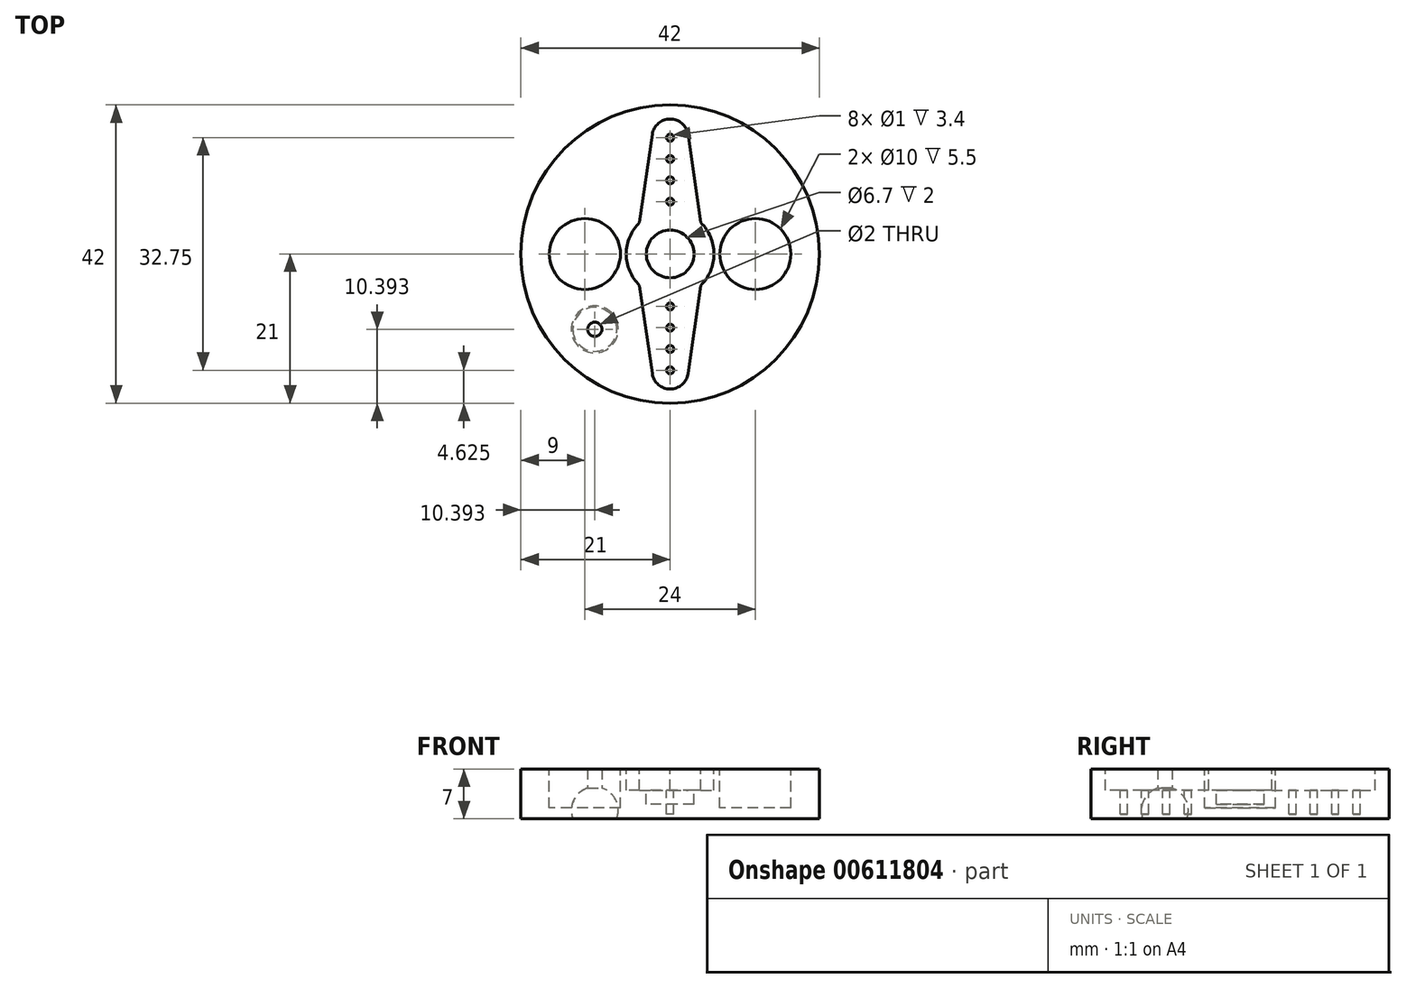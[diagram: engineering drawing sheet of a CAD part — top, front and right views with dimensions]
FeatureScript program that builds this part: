
annotation { "Feature Type Name" : "Feature", "Feature Type Description" : "" }
export const myFeature = defineFeature(function(context is Context, id is Id, definition is map)
    precondition{}
    {
        {
            var Q0;
            Q0=qCreatedBy(makeId("Top.planeOp"),FACE);
            var sketch = newSketch(context, id + "F0", { "sketchPlane" : qUnion([Q0])});
            skCircle(sketch, "E0", {"center": v(0, 0) * mm, "radius": 21 * mm});
            skSolve(sketch);
        }
        {
            var Q0;
            Q0=makeQuery(id+"F0.imprint","IMPRINT",FACE,{"disambiguationData":[TD([[makeQuery(id+"F0.imprint","IMPRINT",EDGE,{"derivedFrom":sQuery(id+"F0.wireOp",EDGE,"E0")}),1.0]])]});
            extrude(context, id + "F1", {"entities" : qUnion([Q0]), "depth" : 7 * mm, "offsetDistance" : 25 * mm});
        }
        {
            var Q0;
            Q0=makeQuery(id+"F1.opExtrude","CAP_FACE",FACE,{"disambiguationData":[OSD([sQuery(id+"F0.wireOp",EDGE,"E0")])],"isStart":false});
            var sketch = newSketch(context, id + "F2", { "sketchPlane" : qUnion([Q0])});
            skArc(sketch, "E1", {"start": v(-4.3, 4.43) * mm, "mid": v(-6.17, 0) * mm, "end": v(-4.3, -4.43) * mm});
            skLineSegment(sketch, "E2", {"start": v(0, 19) * mm, "end": v(0, -19) * mm, "construction": true});
            skLineSegment(sketch, "E3", {"start": v(-4.3, 4.43) * mm, "end": v(-2.5, 16.86) * mm});
            skLineSegment(sketch, "E4", {"start": v(-4.3, 4.43) * mm, "end": v(0, 4.43) * mm, "construction": true});
            skLineSegment(sketch, "E5", {"start": v(-2.5, 16.86) * mm, "end": v(0, 16.86) * mm, "construction": true});
            skArc(sketch, "E6", {"start": v(0, 19) * mm, "mid": v(-1.65, 18.4) * mm, "end": v(-2.5, 16.86) * mm});
            skLineSegment(sketch, "E7.MirrorCS", {"start": v(4.3, 4.43) * mm, "end": v(2.5, 16.86) * mm});
            skArc(sketch, "E8.MirrorCS", {"start": v(0, 19) * mm, "mid": v(1.65, 18.4) * mm, "end": v(2.5, 16.86) * mm});
            skLineSegment(sketch, "E9", {"start": v(-21, 0) * mm, "end": v(21, 0) * mm, "construction": true});
            skLineSegment(sketch, "E10.MirrorCS", {"start": v(-4.3, -4.43) * mm, "end": v(-2.5, -16.86) * mm});
            skLineSegment(sketch, "E11.MirrorCS", {"start": v(4.3, -4.43) * mm, "end": v(2.5, -16.86) * mm});
            skArc(sketch, "E12.MirrorCS", {"start": v(0, -19) * mm, "mid": v(-1.65, -18.4) * mm, "end": v(-2.5, -16.86) * mm});
            skArc(sketch, "E13.MirrorCS", {"start": v(0, -19) * mm, "mid": v(1.65, -18.4) * mm, "end": v(2.5, -16.86) * mm});
            skArc(sketch, "E14.trimOffspring", {"start": v(4.3, -4.43) * mm, "mid": v(6.17, 0) * mm, "end": v(4.3, 4.43) * mm});
            skSolve(sketch);
        }
        {
            var Q0;
            Q0 = qSketchRegion(id + "F2", true);
            extrude(context, id + "F3", {"entities" : qUnion([Q0]), "operationType" : NewBodyOperationType.REMOVE, "oppositeDirection" : true, "depth" : 3 * mm, "offsetDistance" : 25 * mm});
        }
        {
            var Q0;
            Q0=makeQuery(id+"F3.boolean.opBoolean","COPY",FACE,{"derivedFrom":makeQuery(id+"F3.opExtrude","CAP_FACE",FACE,{"disambiguationData":[OSD([sQuery(id+"F2.wireOp",EDGE,"E1"),sQuery(id+"F2.wireOp",EDGE,"E3"),sQuery(id+"F2.wireOp",EDGE,"E6"),sQuery(id+"F2.wireOp",EDGE,"E7.MirrorCS"),sQuery(id+"F2.wireOp",EDGE,"E8.MirrorCS"),sQuery(id+"F2.wireOp",EDGE,"E10.MirrorCS"),sQuery(id+"F2.wireOp",EDGE,"E11.MirrorCS"),sQuery(id+"F2.wireOp",EDGE,"E12.MirrorCS"),sQuery(id+"F2.wireOp",EDGE,"E13.MirrorCS"),sQuery(id+"F2.wireOp",EDGE,"E14.trimOffspring")])],"isStart":false})});
            var sketch = newSketch(context, id + "F4", { "sketchPlane" : qUnion([Q0])});
            skArc(sketch, "E15.0", {"start": v(-4.3, 4.43) * mm, "mid": v(-6.17, 0) * mm, "end": v(-4.3, -4.43) * mm, "construction": true});
            skArc(sketch, "E15.1", {"start": v(4.3, -4.43) * mm, "mid": v(6.17, 0) * mm, "end": v(4.3, 4.43) * mm, "construction": true});
            skCircle(sketch, "E16", {"center": v(0, 0) * mm, "radius": 3.35 * mm});
            skSolve(sketch);
        }
        {
            var Q0;
            Q0 = qSketchRegion(id + "F4", true);
            extrude(context, id + "F5", {"entities" : qUnion([Q0]), "operationType" : NewBodyOperationType.REMOVE, "oppositeDirection" : true, "depth" : 2 * mm, "offsetDistance" : 25 * mm});
        }
        {
            var Q0;
            Q0=makeQuery(id+"F3.boolean.opBoolean","COPY",FACE,{"derivedFrom":makeQuery(id+"F3.opExtrude","CAP_FACE",FACE,{"disambiguationData":[OSD([sQuery(id+"F2.wireOp",EDGE,"E1"),sQuery(id+"F2.wireOp",EDGE,"E3"),sQuery(id+"F2.wireOp",EDGE,"E6"),sQuery(id+"F2.wireOp",EDGE,"E7.MirrorCS"),sQuery(id+"F2.wireOp",EDGE,"E8.MirrorCS"),sQuery(id+"F2.wireOp",EDGE,"E10.MirrorCS"),sQuery(id+"F2.wireOp",EDGE,"E11.MirrorCS"),sQuery(id+"F2.wireOp",EDGE,"E12.MirrorCS"),sQuery(id+"F2.wireOp",EDGE,"E13.MirrorCS"),sQuery(id+"F2.wireOp",EDGE,"E14.trimOffspring")])],"isStart":false})});
            var sketch = newSketch(context, id + "F6", { "sketchPlane" : qUnion([Q0])});
            skLineSegment(sketch, "E17", {"start": v(0, 0) * mm, "end": v(0, 19) * mm, "construction": true});
            skCircle(sketch, "E18", {"center": v(0, 7.38) * mm, "radius": 0.5 * mm});
            skCircle(sketch, "E19", {"center": v(0, 10.38) * mm, "radius": 0.5 * mm});
            skCircle(sketch, "E20", {"center": v(0, 13.38) * mm, "radius": 0.5 * mm});
            skCircle(sketch, "E21", {"center": v(0, 16.38) * mm, "radius": 0.5 * mm});
            skLineSegment(sketch, "E22", {"start": v(-21.03, 0) * mm, "end": v(20.98, 0) * mm, "construction": true});
            skCircle(sketch, "E23.MirrorC", {"center": v(0, -7.38) * mm, "radius": 0.5 * mm});
            skCircle(sketch, "E24.MirrorC", {"center": v(0, -10.38) * mm, "radius": 0.5 * mm});
            skCircle(sketch, "E25.MirrorC", {"center": v(0, -13.38) * mm, "radius": 0.5 * mm});
            skCircle(sketch, "E26.MirrorC", {"center": v(0, -16.38) * mm, "radius": 0.5 * mm});
            skSolve(sketch);
        }
        {
            var Q0;
            Q0 = qSketchRegion(id + "F6", true);
            extrude(context, id + "F7", {"entities" : qUnion([Q0]), "operationType" : NewBodyOperationType.REMOVE, "oppositeDirection" : true, "depth" : 3.4 * mm, "offsetDistance" : 25 * mm});
        }
        {
            var Q0;
            Q0=makeQuery(id+"F1.opExtrude","CAP_FACE",FACE,{"disambiguationData":[OSD([sQuery(id+"F0.wireOp",EDGE,"E0")])],"isStart":false});
            var sketch = newSketch(context, id + "F8", { "sketchPlane" : qUnion([Q0])});
            skLineSegment(sketch, "E27", {"start": v(-21, 0) * mm, "end": v(21, 0) * mm, "construction": true});
            skCircle(sketch, "E28", {"center": v(-12, 0) * mm, "radius": 5 * mm});
            skLineSegment(sketch, "E29", {"start": v(0, 21) * mm, "end": v(0, -21) * mm, "construction": true});
            skCircle(sketch, "E30.MirrorC", {"center": v(12, 0) * mm, "radius": 5 * mm});
            skSolve(sketch);
        }
        {
            var Q0;
            Q0 = qSketchRegion(id + "F8", true);
            var Q1;
            Q1=makeQuery(id+"F1.opExtrude","CAP_FACE",FACE,{"disambiguationData":[OSD([sQuery(id+"F0.wireOp",EDGE,"E0")])],"isStart":true});
            extrude(context, id + "F9", {"entities" : qUnion([Q0]), "operationType" : NewBodyOperationType.REMOVE, "endBound" : BoundingType.UP_TO_SURFACE, "oppositeDirection" : true, "depth" : 25 * mm, "endBoundEntityFace" : qUnion([Q1]), "hasOffset" : true, "offsetDistance" : 1.5 * mm});
        }
        {
            var Q0;
            Q0=makeQuery(id+"F1.opExtrude","CAP_FACE",FACE,{"disambiguationData":[OSD([sQuery(id+"F0.wireOp",EDGE,"E0")])],"isStart":false});
            var sketch = newSketch(context, id + "F10", { "sketchPlane" : qUnion([Q0])});
            skLineSegment(sketch, "E31", {"start": v(14.85, 14.85) * mm, "end": v(-14.85, -14.85) * mm});
            skLineSegment(sketch, "E32", {"start": v(0, 0) * mm, "end": v(0, -21) * mm});
            skPoint(sketch, "E33", {"position": v(-10.6, -10.6) * mm});
            skSolve(sketch);
        }
        {
            var Q0;
            Q0=sQuery(id+"F10.wireOp",VERTEX,"E33");
            var Q1;
            Q1=qCreatedBy(makeId("Front.planeOp"),FACE);
            cPlane(context, id + "F11", {"entities" : qUnion([Q0, Q1]), "cplaneType" : CPlaneType.PLANE_POINT, "offset" : 25 * mm, "width" : 150 * mm, "height" : 150 * mm});
        }
        {
            var Q0;
            Q0=qCreatedBy(id+"F11.planeOp",FACE);
            var sketch = newSketch(context, id + "F12", { "sketchPlane" : qUnion([Q0])});
            skLineSegment(sketch, "E34", {"start": v(-10.6, 7) * mm, "end": v(-10.6, 0) * mm});
            skArc(sketch, "E35", {"start": v(-11.6, 4.3) * mm, "mid": v(-13.87, 0.64) * mm, "end": v(-10.6, -2.15) * mm});
            skLineSegment(sketch, "E36", {"start": v(-11.6, 4.3) * mm, "end": v(-11.6, 7) * mm});
            skLineSegment(sketch, "E37", {"start": v(-11.6, 7) * mm, "end": v(-10.6, 7) * mm});
            skLineSegment(sketch, "E38", {"start": v(-10.6, 0) * mm, "end": v(-10.6, -2.15) * mm});
            skSolve(sketch);
        }
        {
            var Q0;
            Q0 = qSketchRegion(id + "F12", true);
            var Q1;
            Q1=sQuery(id+"F12.wireOp",EDGE,"E38");
            revolve(context, id + "F13", {"operationType" : NewBodyOperationType.REMOVE, "entities" : qUnion([Q0]), "axis" : qUnion([Q1]), "revolveType" : RevolveType.FULL, "oppositeDirection" : true});
        }
    });
